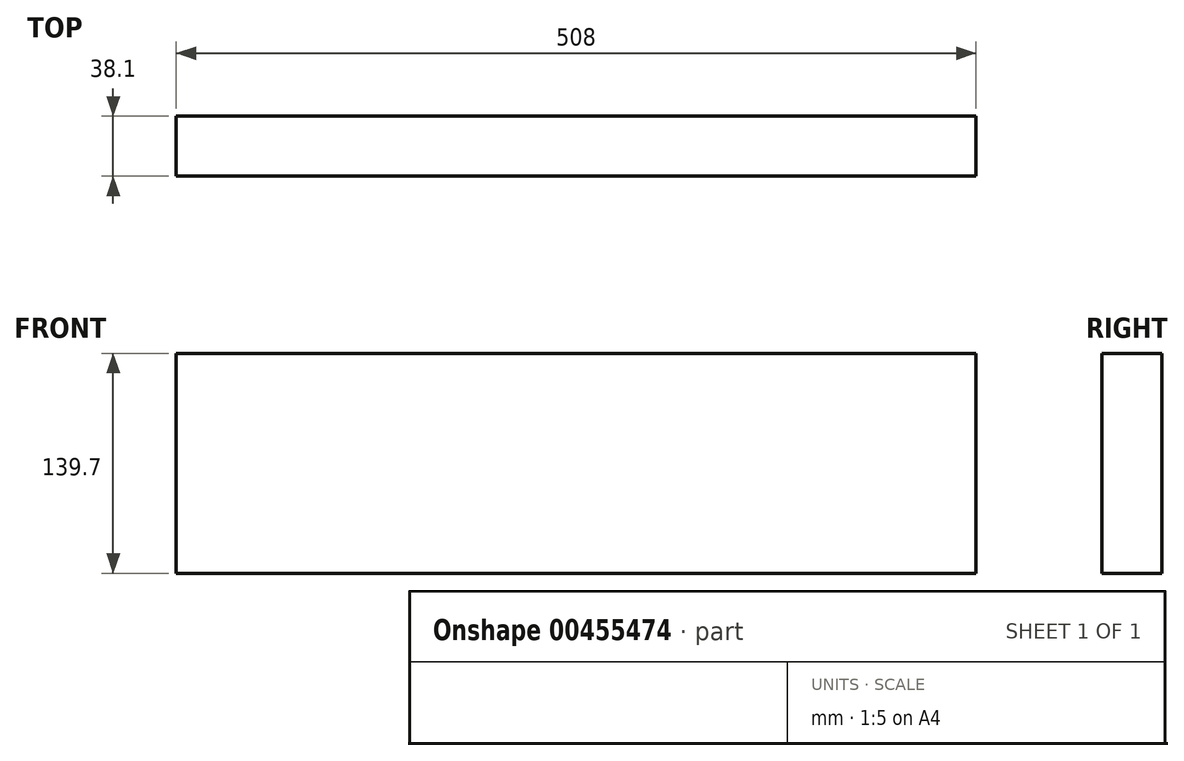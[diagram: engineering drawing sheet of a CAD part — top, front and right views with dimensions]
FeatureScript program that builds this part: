
annotation { "Feature Type Name" : "Feature", "Feature Type Description" : "" }
export const myFeature = defineFeature(function(context is Context, id is Id, definition is map)
    precondition{}
    {
        {
            var Q0;
            Q0=qCreatedBy(makeId("Front.planeOp"),FACE);
            var sketch = newSketch(context, id + "F0", { "sketchPlane" : qUnion([Q0])});
            skLineSegment(sketch, "E0.bottom", {"start": v(-254, 69.85) * mm, "end": v(254, 69.85) * mm});
            skLineSegment(sketch, "E0.top", {"start": v(-254, -69.85) * mm, "end": v(254, -69.85) * mm});
            skLineSegment(sketch, "E0.left", {"start": v(-254, 69.85) * mm, "end": v(-254, -69.85) * mm});
            skLineSegment(sketch, "E0.right", {"start": v(254, 69.85) * mm, "end": v(254, -69.85) * mm});
            skPoint(sketch, "E0.middle", {"position": v(0, 0) * mm});
            skSolve(sketch);
        }
        {
            var Q0;
            Q0=makeQuery(id+"F0.imprint","IMPRINT",FACE,{"disambiguationData":[TD([[makeQuery(id+"F0.imprint","IMPRINT",EDGE,{"derivedFrom":sQuery(id+"F0.wireOp",EDGE,"E0.bottom")}),-1.0]])]});
            extrude(context, id + "F1", {"entities" : qUnion([Q0]), "depth" : 38.1 * mm});
        }
    });
